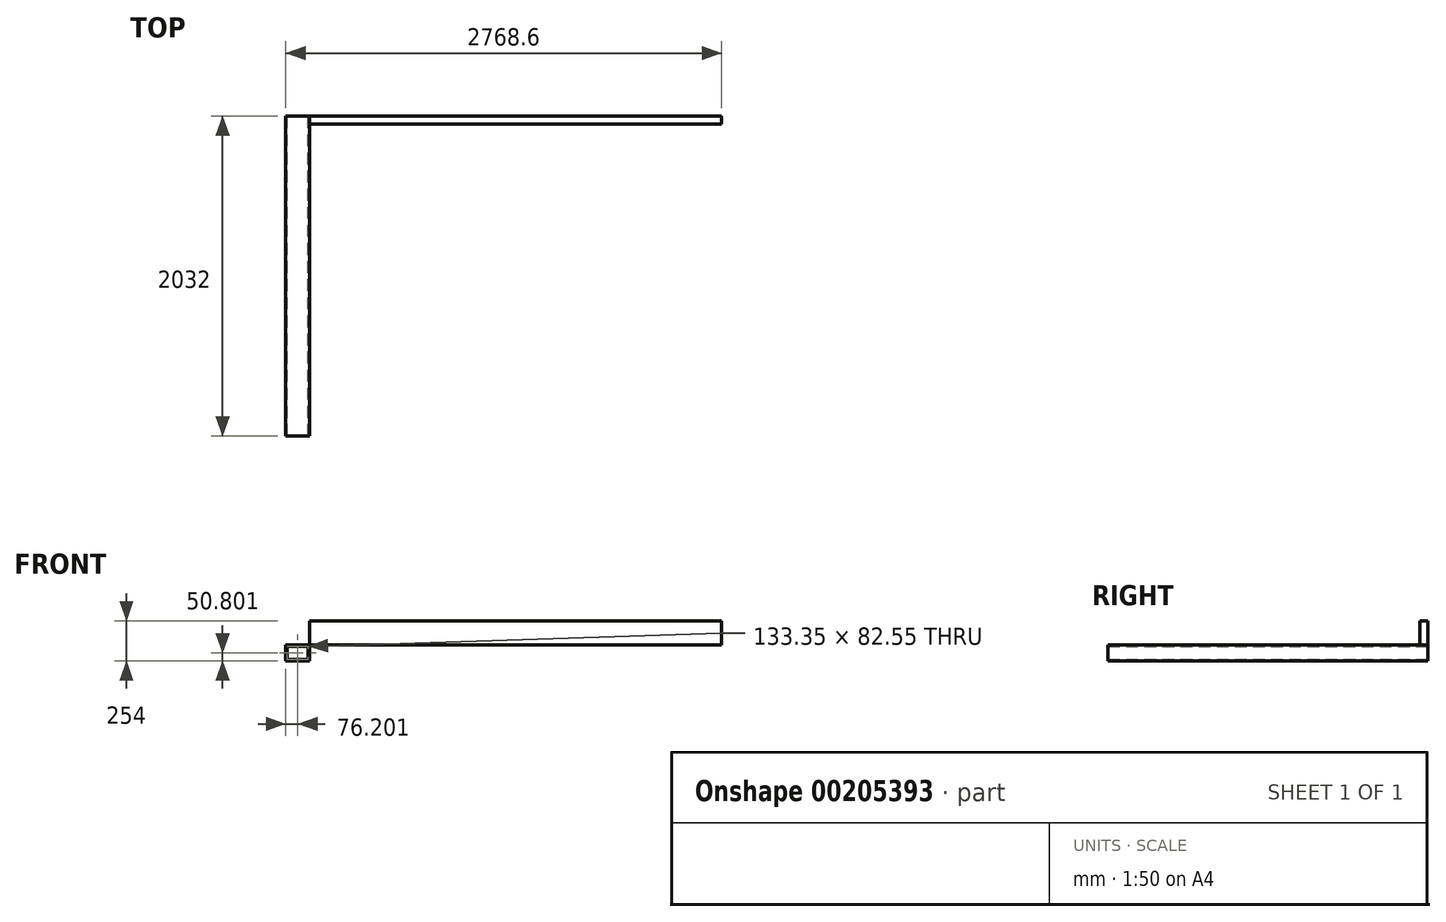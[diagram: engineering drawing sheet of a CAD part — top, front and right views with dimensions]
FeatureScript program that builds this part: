
annotation { "Feature Type Name" : "Feature", "Feature Type Description" : "" }
export const myFeature = defineFeature(function(context is Context, id is Id, definition is map)
    precondition{}
    {
        {
            var Q0;
            Q0=qCreatedBy(makeId("Front.planeOp"),FACE);
            var sketch = newSketch(context, id + "F0", { "sketchPlane" : qUnion([Q0])});
            skLineSegment(sketch, "E0.bottom", {"start": v(-225.94, 87.84) * mm, "end": v(-73.54, 87.84) * mm});
            skLineSegment(sketch, "E0.top", {"start": v(-225.94, -13.76) * mm, "end": v(-73.54, -13.76) * mm});
            skLineSegment(sketch, "E0.left", {"start": v(-225.94, 87.84) * mm, "end": v(-225.94, -13.76) * mm});
            skLineSegment(sketch, "E0.right", {"start": v(-73.54, 87.84) * mm, "end": v(-73.54, -13.76) * mm});
            skLineSegment(sketch, "E1.0", {"start": v(-83.06, 78.32) * mm, "end": v(-83.06, -4.23) * mm});
            skLineSegment(sketch, "E1.1", {"start": v(-216.41, 78.32) * mm, "end": v(-83.06, 78.32) * mm});
            skLineSegment(sketch, "E1.2", {"start": v(-216.41, 78.32) * mm, "end": v(-216.41, -4.23) * mm});
            skLineSegment(sketch, "E1.3", {"start": v(-216.41, -4.23) * mm, "end": v(-83.06, -4.23) * mm});
            skSolve(sketch);
        }
        {
            var Q0;
            Q0=makeQuery(id+"F0.imprint","IMPRINT",FACE,{"disambiguationData":[TD([[makeQuery(id+"F0.imprint","IMPRINT",EDGE,{"derivedFrom":sQuery(id+"F0.wireOp",EDGE,"E0.bottom")}),-1.0]])]});
            extrude(context, id + "F1", {"entities" : qUnion([Q0]), "depth" : 2032 * mm});
        }
        {
            var Q0;
            Q0=makeQuery(id+"F1.opExtrude","SWEPT_FACE",FACE,{"disambiguationData":[OSD([sQuery(id+"F0.wireOp",EDGE,"E0.right")])]});
            var sketch = newSketch(context, id + "F2", { "sketchPlane" : qUnion([Q0])});
            skLineSegment(sketch, "E2", {"start": v(0, 87.84) * mm, "end": v(0, 240.24) * mm});
            skLineSegment(sketch, "E3", {"start": v(0, 240.24) * mm, "end": v(-50.8, 240.24) * mm});
            skLineSegment(sketch, "E4", {"start": v(-50.8, 240.24) * mm, "end": v(-50.8, 87.84) * mm});
            skLineSegment(sketch, "E5", {"start": v(-50.8, 87.84) * mm, "end": v(0, 87.84) * mm});
            skSolve(sketch);
        }
        {
            var Q0;
            Q0 = qSketchRegion(id + "F2", true);
            extrude(context, id + "F3", {"entities" : qUnion([Q0]), "depth" : 2616.2 * mm});
        }
    });
